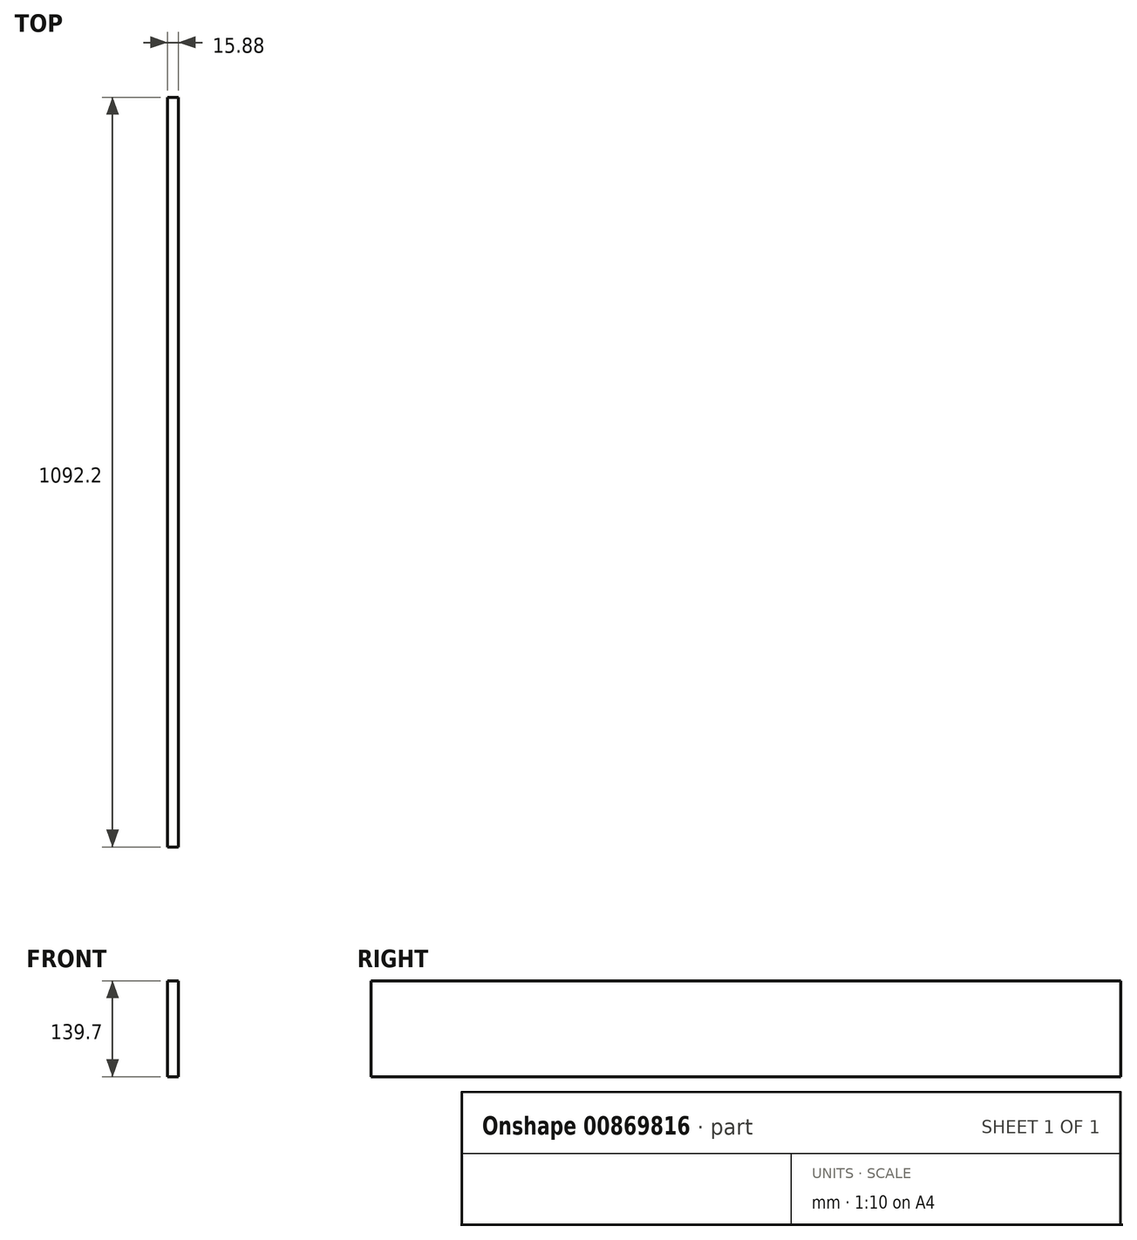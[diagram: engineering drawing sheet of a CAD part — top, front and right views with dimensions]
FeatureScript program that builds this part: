
annotation { "Feature Type Name" : "Feature", "Feature Type Description" : "" }
export const myFeature = defineFeature(function(context is Context, id is Id, definition is map)
    precondition{}
    {
        {
            var Q0;
            Q0=qCreatedBy(makeId("Front.planeOp"),FACE);
            var sketch = newSketch(context, id + "F0", { "sketchPlane" : qUnion([Q0])});
            skLineSegment(sketch, "E0.bottom", {"start": v(7.94, -69.85) * mm, "end": v(-7.94, -69.85) * mm});
            skLineSegment(sketch, "E0.top", {"start": v(7.94, 69.85) * mm, "end": v(-7.94, 69.85) * mm});
            skLineSegment(sketch, "E0.left", {"start": v(7.94, -69.85) * mm, "end": v(7.94, 69.85) * mm});
            skLineSegment(sketch, "E0.right", {"start": v(-7.94, -69.85) * mm, "end": v(-7.94, 69.85) * mm});
            skPoint(sketch, "E0.middle", {"position": v(0, 0) * mm});
            skSolve(sketch);
        }
        {
            var Q0;
            Q0 = qSketchRegion(id + "F0", true);
            extrude(context, id + "F1", {"entities" : qUnion([Q0]), "depth" : 1092.2 * mm, "offsetDistance" : 25.4 * mm});
        }
    });
